# Revit family: bimlib_narujnyeblokisistemakondicionirovaniya_mrv-iii-s_5-7hp_haier
name_source: partatom
category: Оборудование
units: mm (PartAtom-declared; Revit-internal decimal feet)

## family parameters
Всегда вертикально = Да
На основе рабочей плоскости = Нет
Общий = Нет
При загрузке вырезать с полостями = Нет
Размер круглого соединителя = Использовать диаметр
Тип детали = Нормальный
Точка расчета площади = Нет

## types (3) — shared parameters
ADSK_URL документации изделия = https://haierproff.ru
ADSK_URL страницы изделия = https://haierproff.ru
ADSK_Версия Revit = 2017
ADSK_Группирование = VRF-системы MRV III - S'
ADSK_Единица измерения = шт.
ADSK_Завод-изготовитель = Haier Group
ADSK_Классификация нагрузок = ОВК
ADSK_Количество = 1
ADSK_Коэффициент мощности = 1
ADSK_Масса = 99
ADSK_Обозначение = MRV III - S'
ADSK_Размер_Высота = 1250 мм
ADSK_Размер_Глубина = 340 мм
ADSK_Размер_Ширина = 960 мм
ADSK_Расход воздуха = 6500.0 м³/ч
BL_BIM library = https://bimlib.pro
HG_URL поставщика = www.haierproff.ru
URL = www.haier.com
Диаметр_Газ = 19.05 мм
Диаметр_Жидкость = 9.52 мм
Заправка хладагента = 3.80 кг
Изготовитель = Haier Group
Производитель компрессора = MITSUBISHI ELECTRIC
Работа на обогрев = Нет
Рабочий диапазон_Обогрев = -15~ 21
Рабочий диапазон_Охлаждение = -5 ~ 48
Тип компрессора = Ротационный
Тип хладагента = R410A
Частота тока = 50 Гц
zero-valued in all types: Отметка по умолчанию

## per-type parameters (varying)
| type | ADSK_Код изделия | ADSK_Количество фаз | ADSK_Наименование | ADSK_Наименование краткое | ADSK_Напряжение | ADSK_Номинальная мощность | ADSK_Полная мощность | Звуковая мощность | Звуковое давление | Обогрев_Потребляемая мощность | Охлаждение_Потребляемая мощность | Теплопроизводительность | Холодопроизводительность |
| AU482FIERA(H)_5HP_HAIER | AU482FIERA(H) | 1 | Наружный блок VRF-системы кондиционирования MRV III - S', 5HP | VRF-системы MRV MRV III - S', 5HP | 230 В | 3980 Вт | 3980 В·А | 69 | 58 | 4 кВт | 4 кВт | 17 кВт | 15 кВт |
| AU48NFIERA(H)_5HP_HAIER | AU48NFIERA(H) | 3 | Наружный блок VRF-системы кондиционирования MRV III - S', 5HP | VRF-системы MRV MRV III - S', 5HP | 400 В | 3980 Вт | 3980 В·А | 69 | 58 | 4 кВт | 4 кВт | 17 кВт | 15 кВт |
| AU60NFIERA(H)_7HP_HAIER | AU60NFIERA(H) | 3 | Наружный блок VRF-системы кондиционирования MRV III - S', 7HP | VRF-системы MRV MRV III - S', 7HP | 400 В | 5190 Вт | 5190 В·А | 70 | 59 | 5 кВт | 5 кВт | 20 кВт | 18 кВт |
